# Revit family: PRD_FrankeWS_SnksSuprts_SiriusUnderframeToUtilitySinks_U701V,U702V
name_source: partatom
category: Plumbing Fixtures
revit_build: Autodesk Revit 2018 (Build: 20190510_1515(x64)
units: mm (PartAtom-declared; Revit-internal decimal feet)

## family parameters
Always vertical = Yes
Cut with Voids When Loaded = No
OmniClass Number = 23.40.20.00
OmniClass Title = General Furniture and Specialties
Part Type = Normal
Room Calculation Point = No
Round Connector Dimension = Use Diameter
Shared = Yes
Work Plane-Based = No

## types (2) — shared parameters
AssetType = Fixed
Category = Pr_20_85_09_88, Sink supports
Color = Stainless steel
DurationUnit = year
Finish = Satin finished
Form = Floor-standing
IfcExportAs = IfcBuildingElementProxy
IfcExportType = NOTDEFINED
Manufacturer = KWC Group AG
ManufacturerName = KWC Group AG
ManufacturerURL = www.kwc.com
Material = Stainless steel
MaterialThickness = 1 mm  [stored 0.00328084 ft]
MaterialsBracketsBody = Stainless steel 1.4301
MaterialsBracketsFinishAndColour = Satin finished
MaterialsLegsBody = Stainless steel 1.4301
MaterialsLegsFinishAndColour = Satin finished
NBSDescription = Supports for sinks
NBSReference = 45-35-70/347
NominalHeight = 870 mm  [stored 2.85433 ft]
NominalWidth = 518 mm  [stored 1.69948 ft]
ProductInformation = https://pim.kwc.com
Shape = Rectangular
URL = www.kwc.com
UnderframeMaterial = PRD_AR_StainlessSteel_SatinFinished
Uniclass2015Code = Pr_20_85_09_88
Uniclass2015Title = Sink supports
Uniclass2015Version = Products v1.5
Version = 1
WarrantyDurationUnit = year

## per-type parameters (varying)
| type | BIMObjectName | Description | Features | GrossWeight | Length | ModelNumber | Name | NetWeight | NominalLength | Size |
| U701V | PRD_AR_SinkSupports_SiriusUnderframeToUtilitySinks_U701V | Stainless steel, working height 900mm including commercial sink. Apron 300 mm deep on all sides. Four adjustable feet. Underframe in supply fragmented. dimensions 1040 x 870 x 518 mm (W x H x D), for BS351 and BS352 | stainless steel, 1.00 mm, satin finished, no mounting, 1040x870x518 mm (WxHxD) | 34.50 kg | 1040 mm  [stored 3.41207 ft] | 2000100784 | SIRIUS underframe to utility sinks U701V | 14.50 kg | 1040 mm  [stored 3.41207 ft] | 1040 x 870 x 518 mm |
| U702V | PRD_AR_SinkSupports_SiriusUnderframeToUtilitySinks_U702V | Stainless steel, working height 900mm including commercial sink. Apron 300 mm deep on all sides. Four adjustable feet. Underframe in supply fragmented. dimensions 2140 x 870 x 518 mm (W x H x D), for BS353 | stainless steel, 1.00 mm, satin finished, no mounting, 2140x870x518 mm (WxHxD) | 42.00 kg | 2140 mm  [stored 7.021 ft] | 2000100785 | SIRIUS underframe to utility sinks U702V | 22.00 kg | 2140 mm  [stored 7.021 ft] | 2140 x 870 x 518 mm |

note: column(s) folded — value = type name in every type: Model, ModelReference

note: [stored X ft] marks values corroborated as IEEE doubles in the binary element streams (Revit-internal decimal feet)

## geometry (parser evidence)
native form markers: Sweep x2
no freeform markers — native parametric forms only
